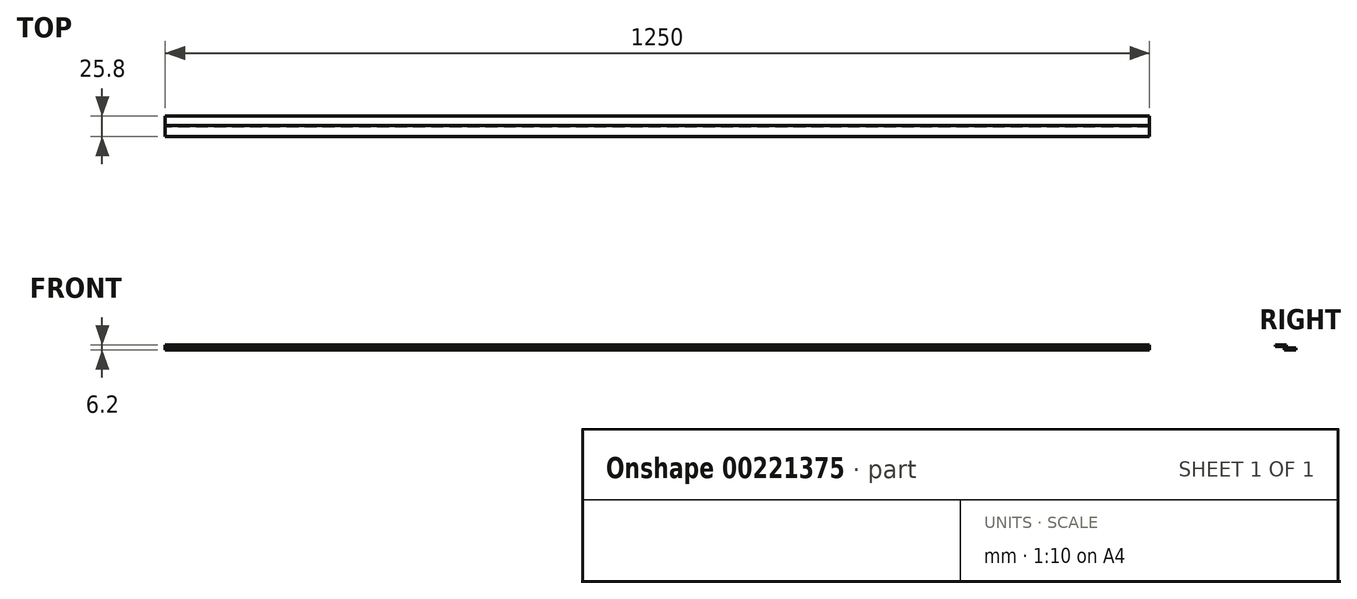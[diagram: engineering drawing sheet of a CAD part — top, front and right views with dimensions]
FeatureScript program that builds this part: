
annotation { "Feature Type Name" : "Feature", "Feature Type Description" : "" }
export const myFeature = defineFeature(function(context is Context, id is Id, definition is map)
    precondition{}
    {
        {
            var Q0;
            Q0=qCreatedBy(makeId("Right.planeOp"),FACE);
            var sketch = newSketch(context, id + "F0", { "sketchPlane" : qUnion([Q0])});
            skLineSegment(sketch, "E0", {"start": v(0, 0) * mm, "end": v(0, -4) * mm});
            skLineSegment(sketch, "E1", {"start": v(0, -4) * mm, "end": v(11.8, -4) * mm});
            skLineSegment(sketch, "E2", {"start": v(11.8, -4) * mm, "end": v(11.8, -6.2) * mm});
            skLineSegment(sketch, "E3", {"start": v(11.8, -6.2) * mm, "end": v(-2.2, -6.2) * mm});
            skLineSegment(sketch, "E4", {"start": v(-2.2, -6.2) * mm, "end": v(-2.2, -2.2) * mm});
            skLineSegment(sketch, "E5", {"start": v(-2.2, -2.2) * mm, "end": v(-14, -2.2) * mm});
            skLineSegment(sketch, "E6", {"start": v(-14, -2.2) * mm, "end": v(-14, 0) * mm});
            skLineSegment(sketch, "E7", {"start": v(-14, 0) * mm, "end": v(0, 0) * mm});
            skSolve(sketch);
        }
        {
            var Q0;
            Q0=qSketchRegion(id+"F0",true);
            extrude(context, id + "F1", {"entities" : qUnion([Q0]), "depth" : 1250 * mm, "symmetric" : true});
        }
    });
